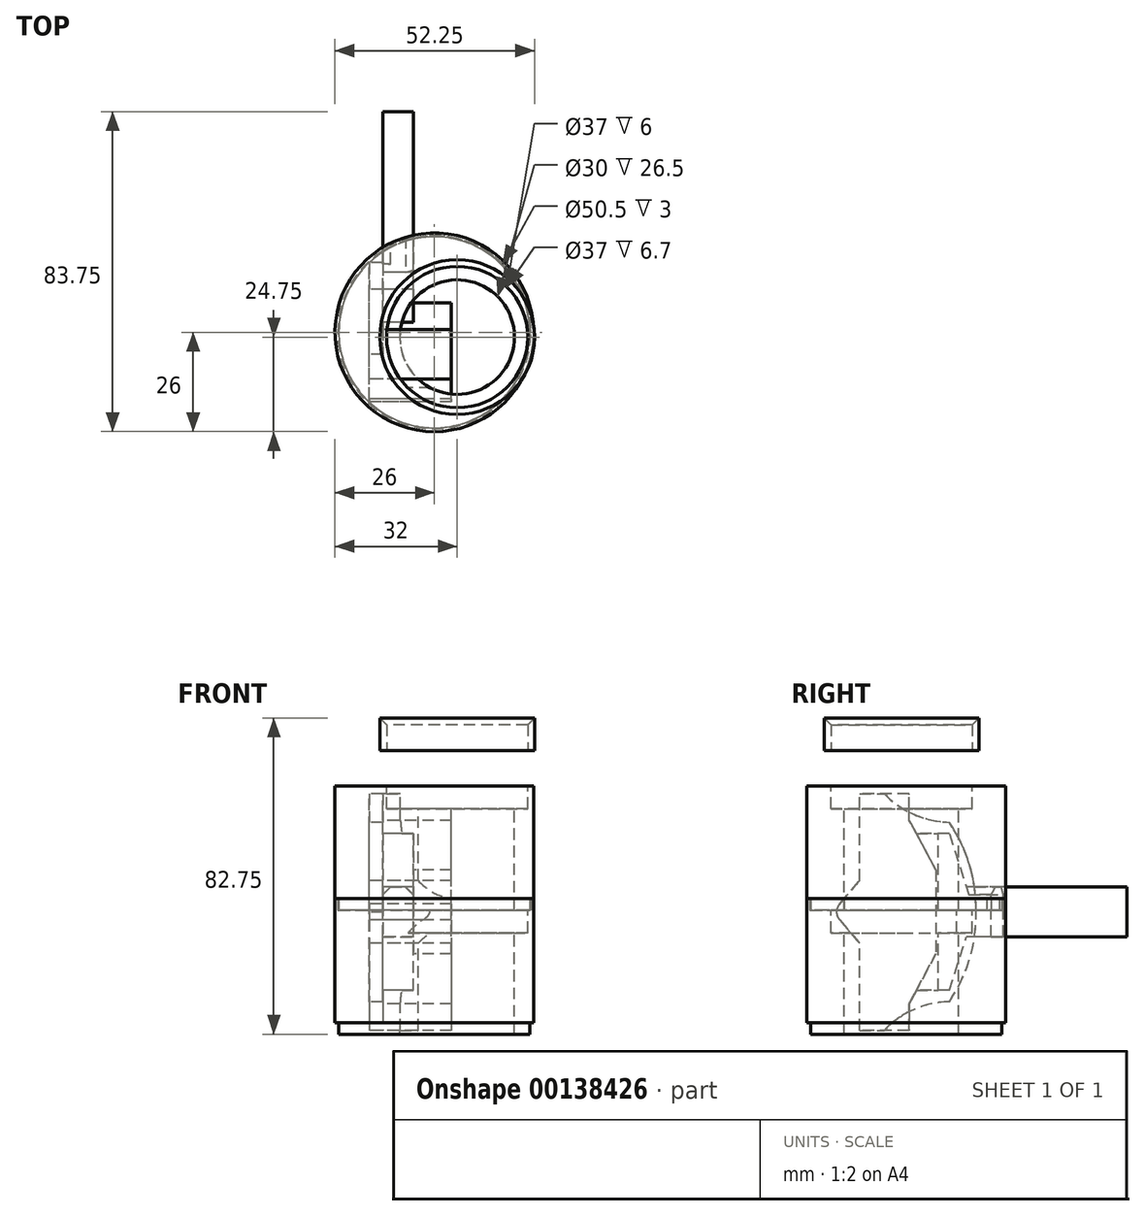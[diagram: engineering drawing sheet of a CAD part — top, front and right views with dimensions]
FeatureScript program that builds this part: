
annotation { "Feature Type Name" : "Feature", "Feature Type Description" : "" }
export const myFeature = defineFeature(function(context is Context, id is Id, definition is map)
    precondition{}
    {
        {
            var Q0;
            Q0=qCreatedBy(makeId("Top.planeOp"),FACE);
            var sketch = newSketch(context, id + "F0", { "sketchPlane" : qUnion([Q0])});
            skLineSegment(sketch, "E0", {"start": v(0, 0) * mm, "end": v(31, 0) * mm});
            skLineSegment(sketch, "E1", {"start": v(31, 0) * mm, "end": v(31, 6.5) * mm});
            skArc(sketch, "E2", {"start": v(23.5, 23.5) * mm, "mid": v(25.55, 14.25) * mm, "end": v(31, 6.5) * mm});
            skArc(sketch, "E3", {"start": v(23.5, 23.5) * mm, "mid": v(12.3, 28.85) * mm, "end": v(0, 30.5) * mm});
            skArc(sketch, "E4", {"start": v(0, -6) * mm, "mid": v(2.12, -5.12) * mm, "end": v(3, -3) * mm});
            skLineSegment(sketch, "E5.MirrorCS", {"start": v(-31, 0) * mm, "end": v(-31, 6.5) * mm});
            skLineSegment(sketch, "E6.MirrorCS", {"start": v(0, 0) * mm, "end": v(-31, 0) * mm});
            skArc(sketch, "E7.MirrorCS", {"start": v(0, -6) * mm, "mid": v(-2.12, -5.12) * mm, "end": v(-3, -3) * mm});
            skArc(sketch, "E8.MirrorCS", {"start": v(-23.5, 23.5) * mm, "mid": v(-12.3, 28.85) * mm, "end": v(0, 30.5) * mm});
            skArc(sketch, "E9.MirrorCS", {"start": v(-23.5, 23.5) * mm, "mid": v(-25.55, 14.25) * mm, "end": v(-31, 6.5) * mm});
            skLineSegment(sketch, "E10", {"start": v(2.12, -5.12) * mm, "end": v(8.22, 0) * mm});
            skLineSegment(sketch, "E11.MirrorCS", {"start": v(-2.12, -5.12) * mm, "end": v(-8.22, 0) * mm});
            skSolve(sketch);
        }
        {
            var Q0;
            Q0 = qSketchRegion(id + "F0", true);
            extrude(context, id + "F1", {"entities" : qUnion([Q0]), "depth" : 3.5 * mm});
        }
        {
            var Q0;
            Q0=makeQuery(id+"F1.opExtrude","CAP_FACE",FACE,{"disambiguationData":[OSD([sQuery(id+"F0.wireOp",EDGE,"E0"),sQuery(id+"F0.wireOp",EDGE,"E1"),sQuery(id+"F0.wireOp",EDGE,"E2"),sQuery(id+"F0.wireOp",EDGE,"E3"),sQuery(id+"F0.wireOp",EDGE,"E4"),sQuery(id+"F0.wireOp",EDGE,"ia1xnNKN-H2uq-UXTB-JHrW-8P8bqhIhne8i"),sQuery(id+"F0.wireOp",EDGE,"4d5fb20d-1073-4855-af24-ff352f3ab0560.MirrorCS"),sQuery(id+"F0.wireOp",EDGE,"E5.MirrorCS"),sQuery(id+"F0.wireOp",EDGE,"E6.MirrorCS"),sQuery(id+"F0.wireOp",EDGE,"E7.MirrorCS"),sQuery(id+"F0.wireOp",EDGE,"E8.MirrorCS"),sQuery(id+"F0.wireOp",EDGE,"E9.MirrorCS")])],"isStart":false});
            var sketch = newSketch(context, id + "F2", { "sketchPlane" : qUnion([Q0])});
            skLineSegment(sketch, "E12.bottom", {"start": v(24, 0) * mm, "end": v(8.22, 0) * mm});
            skLineSegment(sketch, "E12.top", {"start": v(11, 20) * mm, "end": v(0, 20) * mm});
            skLineSegment(sketch, "E12.left", {"start": v(24, 0) * mm, "end": v(24, 13) * mm});
            skPoint(sketch, "E12.middle", {"position": v(0, 10) * mm});
            skLineSegment(sketch, "E13", {"start": v(11, 20) * mm, "end": v(24, 13) * mm});
            skLineSegment(sketch, "E14", {"start": v(0, 20) * mm, "end": v(0, 0) * mm});
            skPoint(sketch, "E12.right.end.orphan", {"position": v(-24, 20) * mm});
            skPoint(sketch, "E15.orphan", {"position": v(-24, 0) * mm});
            skPoint(sketch, "E16.orphan", {"position": v(24, 20) * mm});
            skLineSegment(sketch, "E17.MirrorCS", {"start": v(-11, 20) * mm, "end": v(-24, 13) * mm});
            skLineSegment(sketch, "E18.MirrorCS", {"start": v(-24, 0) * mm, "end": v(-8.22, 0) * mm});
            skLineSegment(sketch, "E19.MirrorCS", {"start": v(-11, 20) * mm, "end": v(0, 20) * mm});
            skLineSegment(sketch, "E20.MirrorCS", {"start": v(-24, 0) * mm, "end": v(-24, 13) * mm});
            skLineSegment(sketch, "E21.bottom", {"start": v(-6.5, 20) * mm, "end": v(6.5, 20) * mm});
            skArc(sketch, "E22", {"start": v(0, -6) * mm, "mid": v(1.15, -5.77) * mm, "end": v(2.12, -5.12) * mm});
            skLineSegment(sketch, "E23", {"start": v(2.12, -5.12) * mm, "end": v(8.22, 0) * mm});
            skLineSegment(sketch, "E24.MirrorCS", {"start": v(-2.12, -5.12) * mm, "end": v(-8.22, 0) * mm});
            skArc(sketch, "E25.MirrorCS", {"start": v(0, -6) * mm, "mid": v(-1.15, -5.77) * mm, "end": v(-2.12, -5.12) * mm});
            skLineSegment(sketch, "E26.bottom", {"start": v(-24, 13) * mm, "end": v(-31, 13) * mm});
            skLineSegment(sketch, "E26.top", {"start": v(-24, 0) * mm, "end": v(-31, 0) * mm});
            skLineSegment(sketch, "E26.left", {"start": v(-24, 13) * mm, "end": v(-24, 0) * mm});
            skLineSegment(sketch, "E26.right", {"start": v(-31, 13) * mm, "end": v(-31, 0) * mm});
            skLineSegment(sketch, "E27.bottom", {"start": v(24, 13) * mm, "end": v(31, 13) * mm});
            skLineSegment(sketch, "E27.top", {"start": v(24, 0) * mm, "end": v(31, 0) * mm});
            skLineSegment(sketch, "E27.left", {"start": v(24, 13) * mm, "end": v(24, 0) * mm});
            skLineSegment(sketch, "E27.right", {"start": v(31, 13) * mm, "end": v(31, 0) * mm});
            skSolve(sketch);
        }
        {
            var Q0;
            Q0 = qSketchRegion(id + "F2", true);
            extrude(context, id + "F3", {"entities" : qUnion([Q0]), "operationType" : NewBodyOperationType.ADD, "depth" : 18 * mm});
        }
        {
            var Q0;
            {var subQ1=sQuery(id+"F0.wireOp",EDGE,"E3");var subQ5=sQuery(id+"F0.wireOp",EDGE,"E2");Q0=makeQuery(id+"F6.boolean.opBoolean","SPLIT",FACE,{"disambiguationData":[TD([makeQuery(id+"F1.opExtrude","SWEPT_FACE",FACE,{"disambiguationData":[OSD([subQ5])]})])],"derivedFrom":makeQuery(id+"F1.opExtrude","CAP_FACE",FACE,{"disambiguationData":[OSD([sQuery(id+"F0.wireOp",EDGE,"E0"),sQuery(id+"F0.wireOp",EDGE,"E1"),subQ5,subQ1,sQuery(id+"F0.wireOp",EDGE,"E4"),sQuery(id+"F0.wireOp",EDGE,"E5.MirrorCS"),sQuery(id+"F0.wireOp",EDGE,"E6.MirrorCS"),sQuery(id+"F0.wireOp",EDGE,"E7.MirrorCS"),sQuery(id+"F0.wireOp",EDGE,"E8.MirrorCS"),sQuery(id+"F0.wireOp",EDGE,"E9.MirrorCS"),sQuery(id+"F0.wireOp",EDGE,"E10"),sQuery(id+"F0.wireOp",EDGE,"E11.MirrorCS")])],"isStart":false})});}
            cPlane(context, id + "F4", {"entities" : qUnion([Q0]), "cplaneType" : CPlaneType.OFFSET, "offset" : 0 * mm, "width" : 150 * mm, "height" : 150 * mm});
        }
        {
            var Q0;
            Q0=qCreatedBy(id+"F4.planeOp",FACE);
            var sketch = newSketch(context, id + "F5", { "sketchPlane" : qUnion([Q0])});
            skLineSegment(sketch, "E28.bottom", {"start": v(-6.5, 70) * mm, "end": v(6.5, 70) * mm});
            skLineSegment(sketch, "E28.top", {"start": v(-6.5, 20) * mm, "end": v(6.5, 20) * mm});
            skLineSegment(sketch, "E28.left", {"start": v(-6.5, 70) * mm, "end": v(-6.5, 20) * mm});
            skLineSegment(sketch, "E28.right", {"start": v(6.5, 70) * mm, "end": v(6.5, 20) * mm});
            skLineSegment(sketch, "E29", {"start": v(6.5, 20) * mm, "end": v(20.5, 20) * mm});
            skLineSegment(sketch, "E30", {"start": v(20.5, 20) * mm, "end": v(20.5, 23.5) * mm});
            skLineSegment(sketch, "E31", {"start": v(20.5, 23.5) * mm, "end": v(6.5, 28) * mm});
            skLineSegment(sketch, "E32.MirrorCS", {"start": v(-20.5, 23.5) * mm, "end": v(-6.5, 28) * mm});
            skLineSegment(sketch, "E33.MirrorCS", {"start": v(-20.5, 20) * mm, "end": v(-20.5, 23.5) * mm});
            skLineSegment(sketch, "E34.MirrorCS", {"start": v(-6.5, 20) * mm, "end": v(-20.5, 20) * mm});
            skLineSegment(sketch, "E35", {"start": v(20.5, 20) * mm, "end": v(20.5, 14.88) * mm});
            skLineSegment(sketch, "E36", {"start": v(20.5, 14.88) * mm, "end": v(11, 20) * mm});
            skLineSegment(sketch, "E37.MirrorCS", {"start": v(-20.5, 20) * mm, "end": v(-20.5, 14.88) * mm});
            skLineSegment(sketch, "E38.MirrorCS", {"start": v(-20.5, 14.88) * mm, "end": v(-11, 20) * mm});
            skSolve(sketch);
        }
        {
            var Q0;
            Q0 = qSketchRegion(id + "F5", true);
            extrude(context, id + "F6", {"entities" : qUnion([Q0]), "operationType" : NewBodyOperationType.ADD, "depth" : 8 * mm});
        }
        {
            var Q0;
            Q0=makeQuery(id+"F1.opExtrude","SWEPT_BODY",BODY,{"disambiguationData":[OSD([sQuery(id+"F0.wireOp",EDGE,"E0"),sQuery(id+"F0.wireOp",EDGE,"E1"),sQuery(id+"F0.wireOp",EDGE,"E2"),sQuery(id+"F0.wireOp",EDGE,"E3"),sQuery(id+"F0.wireOp",EDGE,"E4"),sQuery(id+"F0.wireOp",EDGE,"E5.MirrorCS"),sQuery(id+"F0.wireOp",EDGE,"E6.MirrorCS"),sQuery(id+"F0.wireOp",EDGE,"E7.MirrorCS"),sQuery(id+"F0.wireOp",EDGE,"E8.MirrorCS"),sQuery(id+"F0.wireOp",EDGE,"E9.MirrorCS"),sQuery(id+"F0.wireOp",EDGE,"E10"),sQuery(id+"F0.wireOp",EDGE,"E11.MirrorCS")])]});
            var Q1;
            Q1=makeQuery(id+"F1.opExtrude","CAP_EDGE",EDGE,{"disambiguationData":[OSD([sQuery(id+"F0.wireOp",EDGE,"E1")])],"isStart":true});
            transform(context, id + "F7", {"entities" : qUnion([Q0]), "transformType" : TransformType.ROTATION, "transformAxis" : qUnion([Q1]), "angle" : 90 * degree, "makeCopy" : false});
        }
        {
            var Q0;
            Q0=makeQuery(id+"F1.opExtrude","SWEPT_FACE",FACE,{"disambiguationData":[OSD([sQuery(id+"F0.wireOp",EDGE,"E5.MirrorCS")])]});
            cPlane(context, id + "F8", {"entities" : qUnion([Q0]), "cplaneType" : CPlaneType.OFFSET, "offset" : 2 * mm, "width" : 150 * mm, "height" : 150 * mm});
        }
        {
            var Q0;
            Q0=qCreatedBy(id+"F8.planeOp",FACE);
            var sketch = newSketch(context, id + "F9", { "sketchPlane" : qUnion([Q0])});
            skCircle(sketch, "E39", {"center": v(54, 11) * mm, "radius": 15 * mm});
            skLineSegment(sketch, "E40", {"start": v(54, 11) * mm, "end": v(54, 0) * mm});
            skLineSegment(sketch, "E41", {"start": v(54, 0) * mm, "end": v(0, 0) * mm});
            skPoint(sketch, "E42.middle", {"position": v(51.72, 11) * mm});
            skLineSegment(sketch, "E43", {"start": v(75.5, 11) * mm, "end": v(75.5, 11.1) * mm});
            skLineSegment(sketch, "E44", {"start": v(75.5, 11) * mm, "end": v(75.5, 10.9) * mm});
            skCircle(sketch, "E45", {"center": v(48, 12.25) * mm, "radius": 26 * mm});
            skSolve(sketch);
        }
        {
            var Q0;
            Q0 = qSketchRegion(id + "F9", true);
            extrude(context, id + "F10", {"entities" : qUnion([Q0]), "oppositeDirection" : true, "depth" : 32.5 * mm});
        }
        {
            var Q0;
            Q0=makeQuery(id+"F10.opExtrude","CAP_FACE",FACE,{"disambiguationData":[OSD([sQuery(id+"F9.wireOp",EDGE,"E39"),sQuery(id+"F9.wireOp",EDGE,"wrWgTnFv-jgCk-TBaa-vwGy-EEEAkFFq9qhj")])],"isStart":true});
            var sketch = newSketch(context, id + "F11", { "sketchPlane" : qUnion([Q0])});
            skLineSegment(sketch, "E46", {"start": v(0, 0) * mm, "end": v(54, 0) * mm});
            skLineSegment(sketch, "E47", {"start": v(54, 0) * mm, "end": v(54, 11) * mm});
            skCircle(sketch, "E48", {"center": v(54, 11) * mm, "radius": 18.5 * mm});
            skSolve(sketch);
        }
        {
            var Q0;
            Q0 = qSketchRegion(id + "F11", true);
            extrude(context, id + "F12", {"entities" : qUnion([Q0]), "operationType" : NewBodyOperationType.REMOVE, "oppositeDirection" : true, "depth" : 6 * mm});
        }
        {
            var Q0;
            Q0=makeQuery(id+"F10.opExtrude","CAP_FACE",FACE,{"disambiguationData":[OSD([sQuery(id+"F9.wireOp",EDGE,"E39"),sQuery(id+"F9.wireOp",EDGE,"wrWgTnFv-jgCk-TBaa-vwGy-EEEAkFFq9qhj")])],"isStart":true});
            var sketch = newSketch(context, id + "F13", { "sketchPlane" : qUnion([Q0])});
            skLineSegment(sketch, "E49", {"start": v(48, 12.25) * mm, "end": v(48, 0) * mm});
            skLineSegment(sketch, "E50", {"start": v(48, 0) * mm, "end": v(0, 0) * mm});
            skCircle(sketch, "E51", {"center": v(48, 12.25) * mm, "radius": 26 * mm});
            skCircle(sketch, "E52", {"center": v(48, 12.25) * mm, "radius": 25.25 * mm});
            skSolve(sketch);
        }
        {
            var Q0;
            Q0 = qSketchRegion(id + "F13", true);
            extrude(context, id + "F14", {"entities" : qUnion([Q0]), "operationType" : NewBodyOperationType.ADD, "depth" : 3 * mm});
        }
        {
            var Q0;
            Q0=makeQuery(id+"F10.opExtrude","CAP_FACE",FACE,{"disambiguationData":[OSD([sQuery(id+"F9.wireOp",EDGE,"E39"),sQuery(id+"F9.wireOp",EDGE,"wrWgTnFv-jgCk-TBaa-vwGy-EEEAkFFq9qhj")])],"isStart":false});
            var sketch = newSketch(context, id + "F15", { "sketchPlane" : qUnion([Q0])});
            skCircle(sketch, "E53", {"center": v(48, -12.25) * mm, "radius": 26 * mm});
            skCircle(sketch, "E54", {"center": v(48, -12.25) * mm, "radius": 25 * mm});
            skSolve(sketch);
        }
        {
            var Q0;
            Q0 = qSketchRegion(id + "F15", true);
            extrude(context, id + "F16", {"entities" : qUnion([Q0]), "operationType" : NewBodyOperationType.REMOVE, "oppositeDirection" : true, "depth" : 3 * mm});
        }
        {
            var Q0;
            Q0=makeQuery(id+"F10.opExtrude","SWEPT_BODY",BODY,{"disambiguationData":[OSD([sQuery(id+"F9.wireOp",EDGE,"E39"),sQuery(id+"F9.wireOp",EDGE,"wrWgTnFv-jgCk-TBaa-vwGy-EEEAkFFq9qhj")])]});
            transform(context, id + "F17", {"entities" : qUnion([Q0]), "transformType" : TransformType.TRANSLATION_3D, "dx" : 0 * mm, "dy" : 0 * mm, "dz" : -32.5 * mm, "makeCopy" : true});
        }
        {
            var Q0;
            Q0=makeQuery(id+"F1.opExtrude","SWEPT_BODY",BODY,{"disambiguationData":[OSD([sQuery(id+"F0.wireOp",EDGE,"E0"),sQuery(id+"F0.wireOp",EDGE,"E1"),sQuery(id+"F0.wireOp",EDGE,"E2"),sQuery(id+"F0.wireOp",EDGE,"E3"),sQuery(id+"F0.wireOp",EDGE,"E4"),sQuery(id+"F0.wireOp",EDGE,"E5.MirrorCS"),sQuery(id+"F0.wireOp",EDGE,"E6.MirrorCS"),sQuery(id+"F0.wireOp",EDGE,"E7.MirrorCS"),sQuery(id+"F0.wireOp",EDGE,"E8.MirrorCS"),sQuery(id+"F0.wireOp",EDGE,"E9.MirrorCS"),sQuery(id+"F0.wireOp",EDGE,"E10"),sQuery(id+"F0.wireOp",EDGE,"E11.MirrorCS")])]});
            var Q1;
            Q1=makeQuery(id+"F10.opExtrude","SWEPT_BODY",BODY,{"disambiguationData":[OSD([sQuery(id+"F9.wireOp",EDGE,"E39"),sQuery(id+"F9.wireOp",EDGE,"wrWgTnFv-jgCk-TBaa-vwGy-EEEAkFFq9qhj")])]});
            var Q2;
            Q2=makeQuery(id+"F17.opPattern","COPY",BODY,{"derivedFrom":makeQuery(id+"F10.opExtrude","SWEPT_BODY",BODY,{"disambiguationData":[OSD([sQuery(id+"F9.wireOp",EDGE,"E39"),sQuery(id+"F9.wireOp",EDGE,"wrWgTnFv-jgCk-TBaa-vwGy-EEEAkFFq9qhj")])]}),"instanceName":"1"});
            booleanBodies(context, id + "F18", {"operationType" : BooleanOperationType.SUBTRACTION, "tools" : qUnion([Q0]), "targets" : qUnion([Q1, Q2]), "keepTools" : true});
        }
        {
            var Q0;
            Q0=makeQuery(id+"F10.opExtrude","CAP_FACE",FACE,{"disambiguationData":[OSD([sQuery(id+"F9.wireOp",EDGE,"E39"),sQuery(id+"F9.wireOp",EDGE,"wrWgTnFv-jgCk-TBaa-vwGy-EEEAkFFq9qhj")])],"isStart":true});
            var sketch = newSketch(context, id + "F19", { "sketchPlane" : qUnion([Q0])});
            skLineSegment(sketch, "E55", {"start": v(0, 0) * mm, "end": v(54, 0) * mm});
            skLineSegment(sketch, "E56", {"start": v(54, 0) * mm, "end": v(54, 11) * mm});
            skCircle(sketch, "E57", {"center": v(54, 11) * mm, "radius": 18.52 * mm});
            skCircle(sketch, "E58", {"center": v(48, 12.25) * mm, "radius": 26.5 * mm});
            skSolve(sketch);
        }
        {
            var Q0;
            Q0 = qSketchRegion(id + "F19", true);
            extrude(context, id + "F20", {"entities" : qUnion([Q0]), "depth" : 3 * mm});
        }
        {
            var Q0;
            Q0=makeQuery(id+"F20.opExtrude","CAP_FACE",FACE,{"disambiguationData":[OSD([sQuery(id+"F19.wireOp",EDGE,"E57"),sQuery(id+"F19.wireOp",EDGE,"E58")])],"isStart":false});
            var sketch = newSketch(context, id + "F21", { "sketchPlane" : qUnion([Q0])});
            skCircle(sketch, "E59", {"center": v(54, 11) * mm, "radius": 18.5 * mm});
            skCircle(sketch, "E60", {"center": v(54, 11) * mm, "radius": 20.25 * mm});
            skSolve(sketch);
        }
        {
            var Q0;
            Q0 = qSketchRegion(id + "F21", true);
            extrude(context, id + "F22", {"entities" : qUnion([Q0]), "operationType" : NewBodyOperationType.ADD, "depth" : 15 * mm});
        }
        {
            var Q0;
            Q0=makeQuery(id+"F22.opExtrude","CAP_EDGE",EDGE,{"disambiguationData":[OSD([sQuery(id+"F21.wireOp",EDGE,"E59")])],"isStart":false});
            var Q1;
            Q1=makeQuery(id+"F18.opBoolean","COPY",EDGE,{"derivedFrom":makeQuery(id+"F6.opExtrude","CAP_EDGE",EDGE,{"disambiguationData":[OSD([sQuery(id+"F5.wireOp",EDGE,"E28.left")])],"isStart":false})});
            var Q2;
            {var subQ0=sQuery(id+"F5.wireOp",EDGE,"E28.left");Q2=makeQuery(id+"F18.opBoolean","COPY",EDGE,{"derivedFrom":makeQuery(id+"F6.boolean.opBoolean","SPLIT",EDGE,{"disambiguationData":[topologyDisambiguationEdgeConnected([makeQuery(id+"F6.opExtrude","CAP_FACE",FACE,{"disambiguationData":[OSD([sQuery(id+"F5.wireOp",EDGE,"E28.bottom"),sQuery(id+"F5.wireOp",EDGE,"E28.top"),subQ0,sQuery(id+"F5.wireOp",EDGE,"E28.right"),sQuery(id+"F5.wireOp",EDGE,"E29"),sQuery(id+"F5.wireOp",EDGE,"E30"),sQuery(id+"F5.wireOp",EDGE,"E31"),sQuery(id+"F5.wireOp",EDGE,"E32.MirrorCS"),sQuery(id+"F5.wireOp",EDGE,"E33.MirrorCS"),sQuery(id+"F5.wireOp",EDGE,"E34.MirrorCS"),sQuery(id+"F5.wireOp",EDGE,"E35"),sQuery(id+"F5.wireOp",EDGE,"E36"),sQuery(id+"F5.wireOp",EDGE,"E37.MirrorCS"),sQuery(id+"F5.wireOp",EDGE,"E38.MirrorCS")])],"isStart":true})])],"derivedFrom":makeQuery(id+"F6.opExtrude","CAP_EDGE",EDGE,{"disambiguationData":[OSD([subQ0])],"isStart":true})})});}
            chamfer(context, id + "F23", {"entities" : qUnion([Q0, Q1, Q2]), "width" : 2 * mm, "tangentPropagation" : true});
        }
        {
            var Q0;
            Q0=makeQuery(id+"F10.opExtrude","CAP_FACE",FACE,{"disambiguationData":[OSD([sQuery(id+"F9.wireOp",EDGE,"E39"),sQuery(id+"F9.wireOp",EDGE,"E45")])],"isStart":true});
            var sketch = newSketch(context, id + "F24", { "sketchPlane" : qUnion([Q0])});
            skCircle(sketch, "E61", {"center": v(48, 12.25) * mm, "radius": 28.1 * mm});
            skSolve(sketch);
        }
        {
            var Q0;
            Q0 = qSketchRegion(id + "F24", true);
            extrude(context, id + "F25", {"entities" : qUnion([Q0]), "operationType" : NewBodyOperationType.REMOVE, "depth" : 9.3 * mm});
        }
    });
